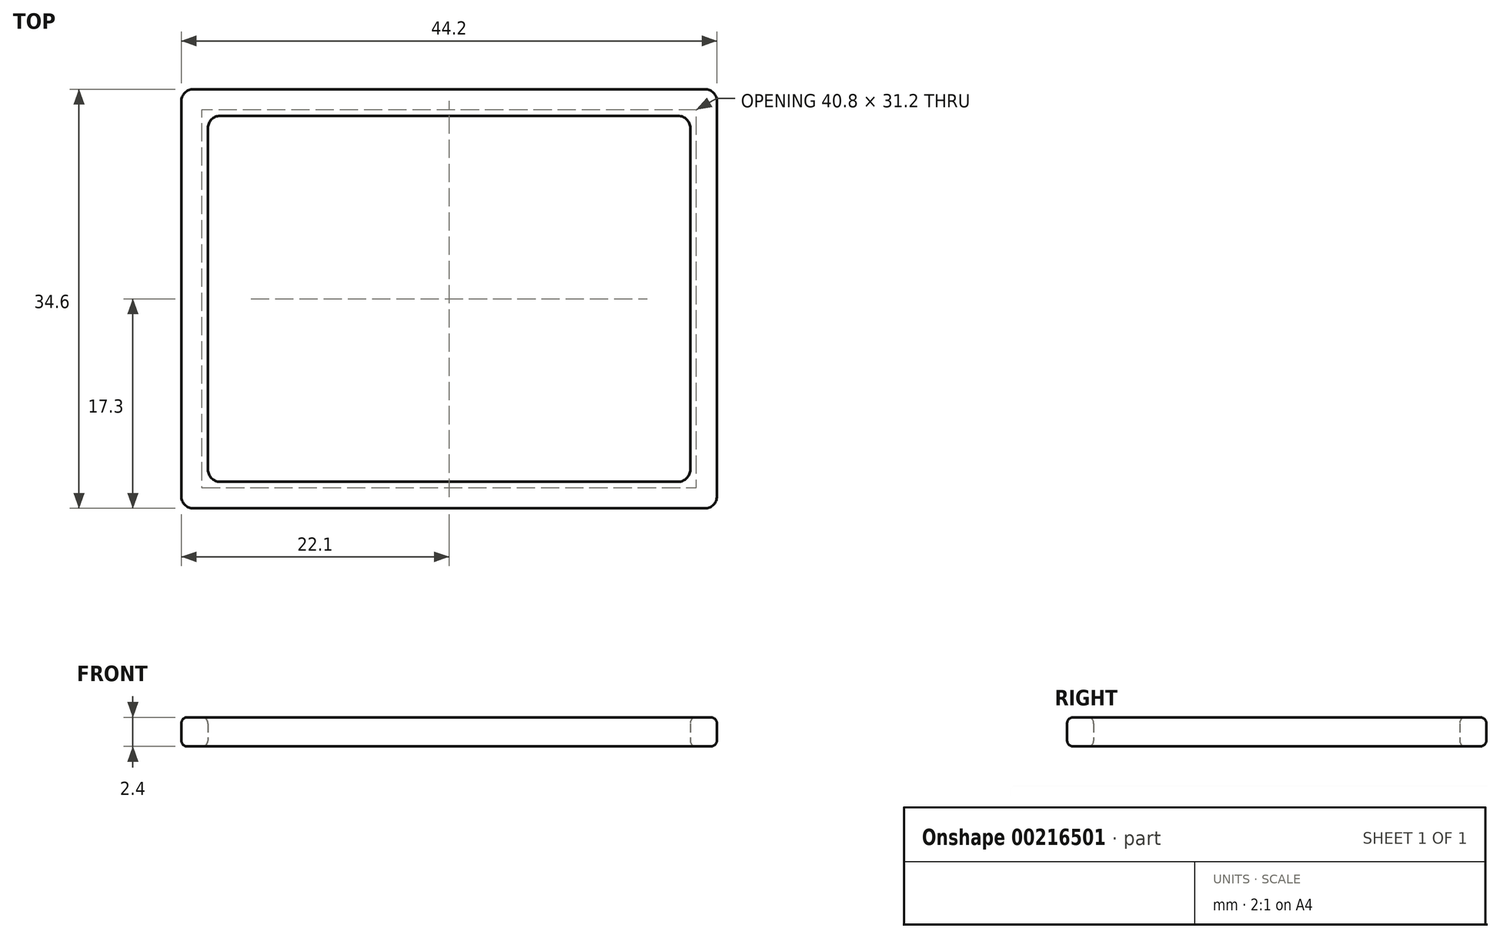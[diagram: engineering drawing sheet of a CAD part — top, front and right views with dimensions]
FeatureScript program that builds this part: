
annotation { "Feature Type Name" : "Feature", "Feature Type Description" : "" }
export const myFeature = defineFeature(function(context is Context, id is Id, definition is map)
    precondition{}
    {
        {
            var Q0;
            Q0=qCreatedBy(makeId("Top.planeOp"),FACE);
            var sketch = newSketch(context, id + "F0", { "sketchPlane" : qUnion([Q0])});
            skLineSegment(sketch, "E0.bottom", {"start": v(22.1, 17.3) * mm, "end": v(-22.1, 17.3) * mm});
            skLineSegment(sketch, "E0.top", {"start": v(22.1, -17.3) * mm, "end": v(-22.1, -17.3) * mm});
            skLineSegment(sketch, "E0.left", {"start": v(22.1, 17.3) * mm, "end": v(22.1, -17.3) * mm});
            skLineSegment(sketch, "E0.right", {"start": v(-22.1, 17.3) * mm, "end": v(-22.1, -17.3) * mm});
            skPoint(sketch, "E0.middle", {"position": v(0, 0) * mm});
            skLineSegment(sketch, "E1.0", {"start": v(-19.9, 15.1) * mm, "end": v(-19.9, -15.1) * mm});
            skLineSegment(sketch, "E1.1", {"start": v(19.9, 15.1) * mm, "end": v(-19.9, 15.1) * mm});
            skLineSegment(sketch, "E1.2", {"start": v(19.9, 15.1) * mm, "end": v(19.9, -15.1) * mm});
            skLineSegment(sketch, "E1.3", {"start": v(19.9, -15.1) * mm, "end": v(-19.9, -15.1) * mm});
            skSolve(sketch);
        }
        {
            var Q0;
            Q0=makeQuery(id+"F0.imprint","IMPRINT",FACE,{"disambiguationData":[TD([[makeQuery(id+"F0.imprint","IMPRINT",EDGE,{"derivedFrom":sQuery(id+"F0.wireOp",EDGE,"E0.bottom")}),1.0]])]});
            extrude(context, id + "F1", {"entities" : qUnion([Q0]), "depth" : 2.4 * mm});
        }
        {
            var Q0;
            Q0=makeQuery(id+"F1.opExtrude","SWEPT_EDGE",EDGE,{"disambiguationData":[OSD([sQuery(id+"F0.wireOp",EDGE,"E0.top"),sQuery(id+"F0.wireOp",EDGE,"E0.left")])]});
            var Q1;
            Q1=makeQuery(id+"F1.opExtrude","SWEPT_EDGE",EDGE,{"disambiguationData":[OSD([sQuery(id+"F0.wireOp",EDGE,"E1.2"),sQuery(id+"F0.wireOp",EDGE,"E1.3")])]});
            var Q2;
            Q2=makeQuery(id+"F1.opExtrude","SWEPT_EDGE",EDGE,{"disambiguationData":[OSD([sQuery(id+"F0.wireOp",EDGE,"E0.top"),sQuery(id+"F0.wireOp",EDGE,"E0.right")])]});
            var Q3;
            Q3=makeQuery(id+"F1.opExtrude","SWEPT_EDGE",EDGE,{"disambiguationData":[OSD([sQuery(id+"F0.wireOp",EDGE,"E1.1"),sQuery(id+"F0.wireOp",EDGE,"E1.2")])]});
            var Q4;
            Q4=makeQuery(id+"F1.opExtrude","SWEPT_EDGE",EDGE,{"disambiguationData":[OSD([sQuery(id+"F0.wireOp",EDGE,"E0.bottom"),sQuery(id+"F0.wireOp",EDGE,"E0.right")])]});
            var Q5;
            Q5=makeQuery(id+"F1.opExtrude","SWEPT_EDGE",EDGE,{"disambiguationData":[OSD([sQuery(id+"F0.wireOp",EDGE,"E1.0"),sQuery(id+"F0.wireOp",EDGE,"E1.1")])]});
            var Q6;
            Q6=makeQuery(id+"F1.opExtrude","SWEPT_EDGE",EDGE,{"disambiguationData":[OSD([sQuery(id+"F0.wireOp",EDGE,"E1.0"),sQuery(id+"F0.wireOp",EDGE,"E1.3")])]});
            var Q7;
            Q7=makeQuery(id+"F1.opExtrude","SWEPT_EDGE",EDGE,{"disambiguationData":[OSD([sQuery(id+"F0.wireOp",EDGE,"E0.bottom"),sQuery(id+"F0.wireOp",EDGE,"E0.left")])]});
            fillet(context, id + "F2", {"entities" : qUnion([Q0, Q1, Q2, Q3, Q4, Q5, Q6, Q7]), "radius" : 1 * mm, "tangentPropagation" : true, "allowEdgeOverflow" : false});
        }
        {
            var Q0;
            Q0=makeQuery(id+"F1.opExtrude","CAP_FACE",FACE,{"disambiguationData":[OSD([sQuery(id+"F0.wireOp",EDGE,"E0.bottom"),sQuery(id+"F0.wireOp",EDGE,"E0.top"),sQuery(id+"F0.wireOp",EDGE,"E0.left"),sQuery(id+"F0.wireOp",EDGE,"E0.right"),sQuery(id+"F0.wireOp",EDGE,"E1.0"),sQuery(id+"F0.wireOp",EDGE,"E1.1"),sQuery(id+"F0.wireOp",EDGE,"E1.2"),sQuery(id+"F0.wireOp",EDGE,"E1.3")])],"isStart":false});
            var Q1;
            Q1=makeQuery(id+"F1.opExtrude","CAP_FACE",FACE,{"disambiguationData":[OSD([sQuery(id+"F0.wireOp",EDGE,"E0.bottom"),sQuery(id+"F0.wireOp",EDGE,"E0.top"),sQuery(id+"F0.wireOp",EDGE,"E0.left"),sQuery(id+"F0.wireOp",EDGE,"E0.right"),sQuery(id+"F0.wireOp",EDGE,"E1.0"),sQuery(id+"F0.wireOp",EDGE,"E1.1"),sQuery(id+"F0.wireOp",EDGE,"E1.2"),sQuery(id+"F0.wireOp",EDGE,"E1.3")])],"isStart":true});
            fillet(context, id + "F3", {"entities" : qUnion([Q0, Q1]), "radius" : 0.5 * mm, "tangentPropagation" : true, "allowEdgeOverflow" : false});
        }
    });
